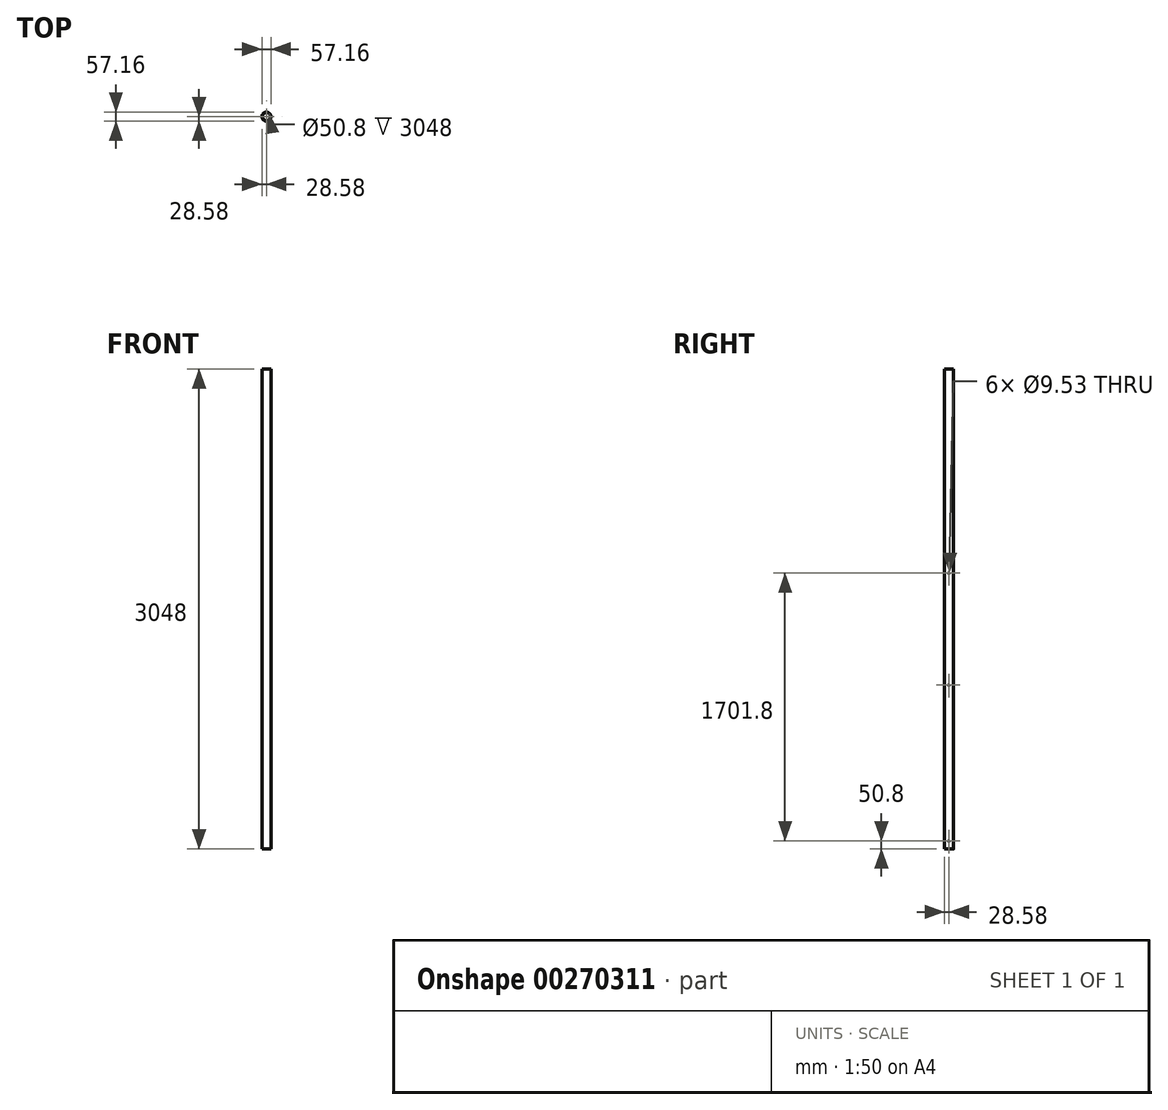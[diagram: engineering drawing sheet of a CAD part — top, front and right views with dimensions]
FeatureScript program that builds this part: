
annotation { "Feature Type Name" : "Feature", "Feature Type Description" : "" }
export const myFeature = defineFeature(function(context is Context, id is Id, definition is map)
    precondition{}
    {
        {
            var Q0;
            Q0=qCreatedBy(makeId("Top.planeOp"),FACE);
            var sketch = newSketch(context, id + "F0", { "sketchPlane" : qUnion([Q0])});
            skCircle(sketch, "E0", {"center": v(0, 0) * mm, "radius": 28.58 * mm});
            skCircle(sketch, "E1", {"center": v(0, 0) * mm, "radius": 25.4 * mm});
            skSolve(sketch);
        }
        {
            var Q0;
            Q0 = qSketchRegion(id + "F0", true);
            extrude(context, id + "F1", {"entities" : qUnion([Q0]), "endBound" : BoundingType.SYMMETRIC, "depth" : 3048 * mm});
        }
        {
            var Q0;
            Q0=qCreatedBy(makeId("Right.planeOp"),FACE);
            var sketch = newSketch(context, id + "F2", { "sketchPlane" : qUnion([Q0])});
            skCircle(sketch, "E2", {"center": v(0, -1473.2) * mm, "radius": 4.76 * mm});
            skCircle(sketch, "E3", {"center": v(0, -482.6) * mm, "radius": 4.76 * mm});
            skCircle(sketch, "E4", {"center": v(0, 228.6) * mm, "radius": 4.76 * mm});
            skSolve(sketch);
        }
        {
            var Q0;
            Q0 = qSketchRegion(id + "F2", true);
            extrude(context, id + "F3", {"entities" : qUnion([Q0]), "operationType" : NewBodyOperationType.REMOVE, "endBound" : BoundingType.SYMMETRIC, "oppositeDirection" : true, "depth" : 101.6 * mm});
        }
    });
